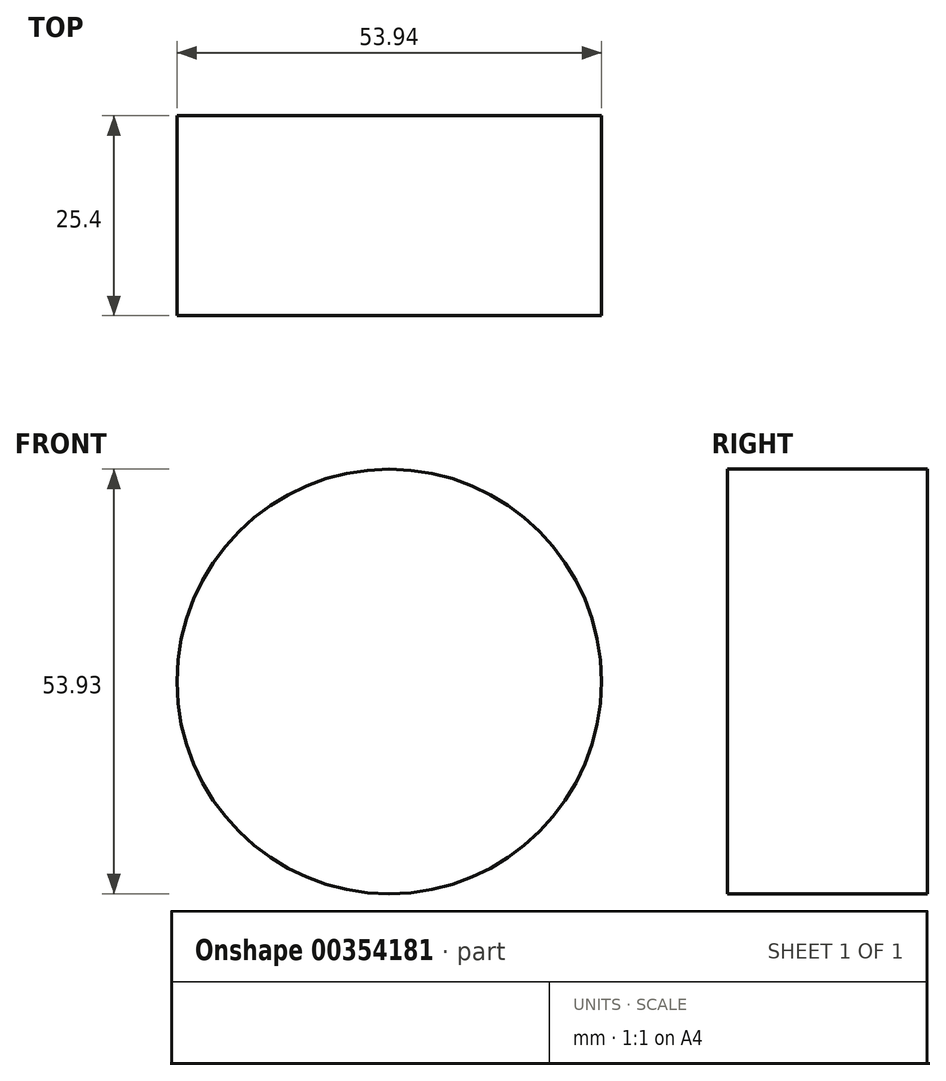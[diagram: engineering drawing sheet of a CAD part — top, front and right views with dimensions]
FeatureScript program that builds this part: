
annotation { "Feature Type Name" : "Feature", "Feature Type Description" : "" }
export const myFeature = defineFeature(function(context is Context, id is Id, definition is map)
    precondition{}
    {
        {
            var Q0;
            Q0=qCreatedBy(makeId("Front.planeOp"),FACE);
            var sketch = newSketch(context, id + "F0", { "sketchPlane" : qUnion([Q0])});
            skCircle(sketch, "E0", {"center": v(-36.51, 29.52) * mm, "radius": 26.97 * mm});
            skSolve(sketch);
        }
        {
            var Q0;
            Q0 = qSketchRegion(id + "F0", true);
            extrude(context, id + "F1", {"entities" : qUnion([Q0]), "depth" : 25.4 * mm});
        }
    });
